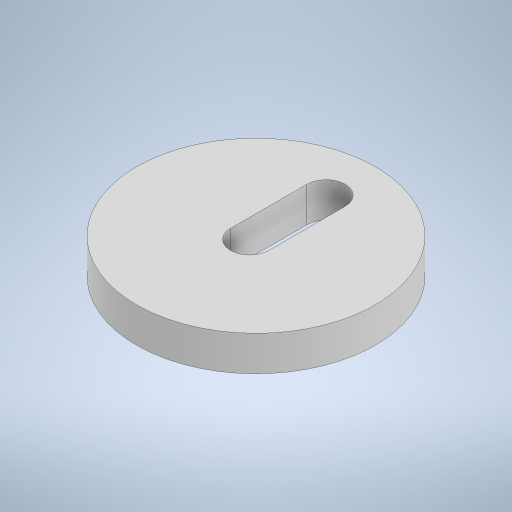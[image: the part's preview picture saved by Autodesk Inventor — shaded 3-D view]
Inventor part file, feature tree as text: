
AUTODESK INVENTOR PART (.ipt)
format: ipt  version: 2024.1 (Build 281209000, 209)  size: 304,640 bytes
history: native  units: mm
features: extrude x2, sketch x2, other x1
ambient origin geometry x8: Origin, YZ Plane, XZ Plane, XY Plane, X Axis, Y Axis, Z Axis, Center Point
bodies: Body1 (feature_tree)
feature tree (5):
  other  "ソリッド1"
  extrude  "押し出し1"  Depth=45.0mm
  extrude  "押し出し2"  Depth=51.0mm
  sketch  "スケッチ1"
  sketch  "スケッチ2"
